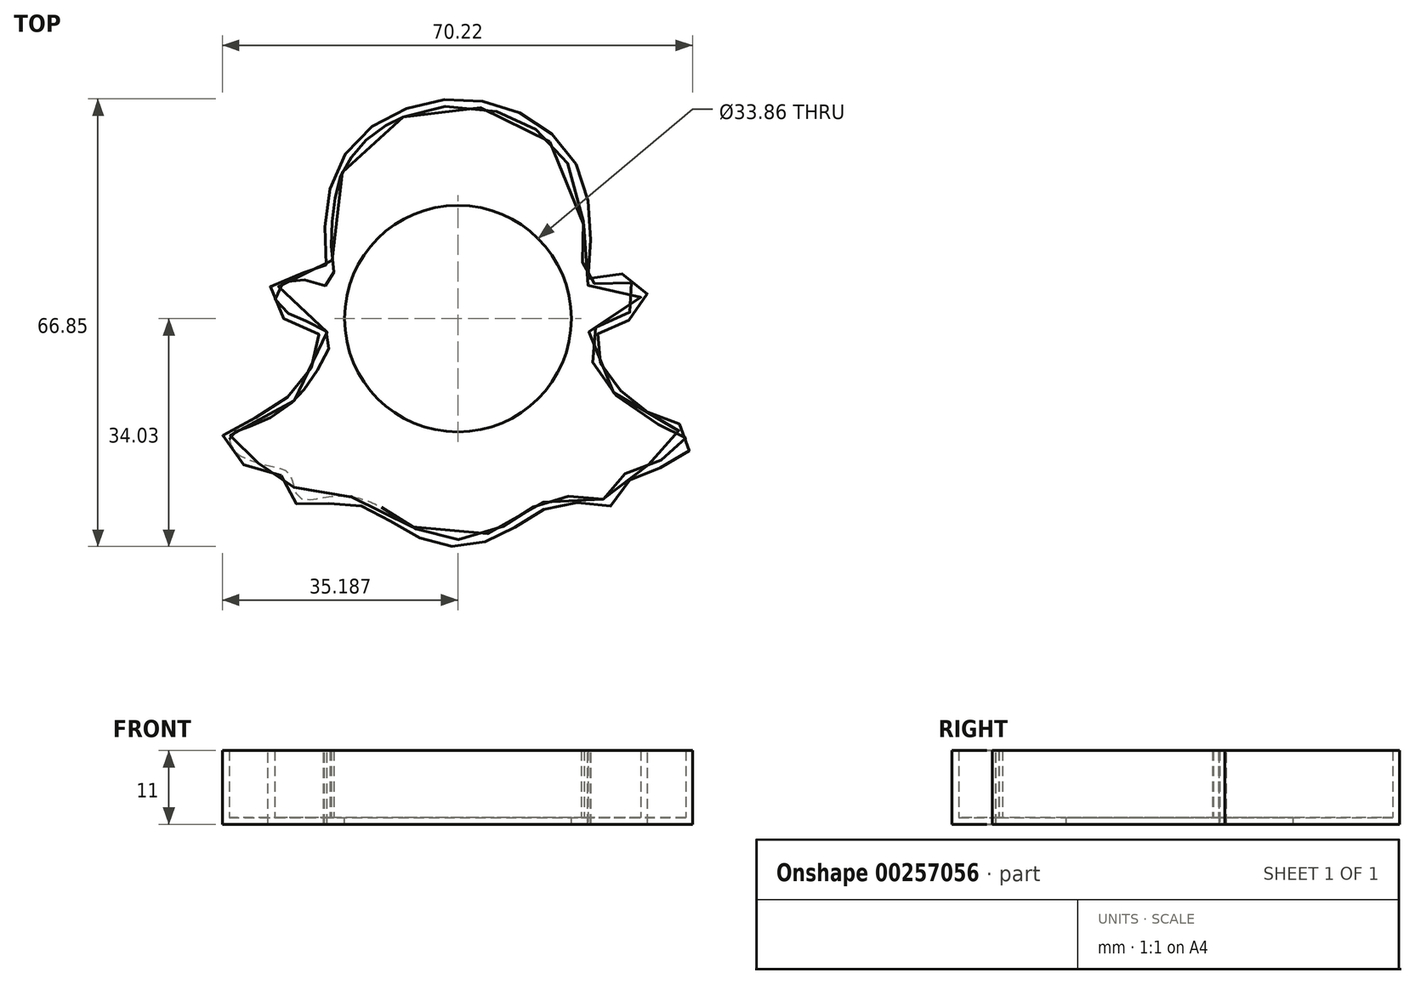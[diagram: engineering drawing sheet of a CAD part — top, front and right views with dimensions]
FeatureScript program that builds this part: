
annotation { "Feature Type Name" : "Feature", "Feature Type Description" : "" }
export const myFeature = defineFeature(function(context is Context, id is Id, definition is map)
    precondition{}
    {
        {
            var Q0;
            Q0=qCreatedBy(makeId("Top.planeOp"),FACE);
            var sketch = newSketch(context, id + "F0", { "sketchPlane" : qUnion([Q0])});
            skFitSpline(sketch, "E0", {"points": [v(3.38, 30.13) * mm, v(1.43, 29.22) * mm, v(-1.52, 27.22) * mm, v(-3.73, 24.97) * mm, v(-5.58, 22.16) * mm, v(-6.38, 19.91) * mm, v(-7.07, 16.23) * mm, v(-7.31, 12.96) * mm, v(-7.22, 8.74) * mm, v(-7.15, 5.54) * mm, v(-8.7, 4.92) * mm, v(-11.6, 5.85) * mm, v(-14.4, 5.54) * mm, v(-15.8, 3.5) * mm, v(-14.95, 1.56) * mm, v(-12.7, 0.26) * mm, v(-10.5, -0.63) * mm, v(-7.93, -2.11) * mm, v(-7.62, -4.06) * mm, v(-9.05, -7.09) * mm, v(-11.09, -10.2) * mm, v(-12.33, -11.65) * mm, v(-14.42, -13.48) * mm, v(-18.32, -15.76) * mm, v(-20.22, -16.3) * mm, v(-21.5, -16.8) * mm, v(-22.14, -17.2) * mm, v(-22.6, -17.69) * mm, v(-22.48, -18.57) * mm, v(-22.12, -19.35) * mm, v(-21.65, -19.92) * mm, v(-21.28, -20.24) * mm, v(-20.78, -20.56) * mm, v(-20.06, -20.9) * mm, v(-18.98, -21.32) * mm, v(-17.82, -21.7) * mm, v(-16.93, -21.92) * mm, v(-16.09, -22.1) * mm, v(-14.96, -22.38) * mm, v(-14.29, -22.62) * mm, v(-13.53, -23.33) * mm, v(-13.13, -24.4) * mm, v(-12.87, -25.45) * mm, v(-12, -26.83) * mm, v(-10.17, -27) * mm, v(-9.12, -26.8) * mm, v(-7.3, -26.52) * mm, v(-4.87, -26.55) * mm, v(-2.83, -26.94) * mm, v(-1.35, -27.46) * mm, v(0.63, -28.45) * mm, v(2.23, -29.52) * mm, v(4.2, -30.82) * mm, v(5.93, -31.7) * mm, v(7.93, -32.53) * mm, v(10.28, -33) * mm, v(13.94, -32.78) * mm, v(16.6, -31.88) * mm, v(18.33, -31.03) * mm, v(19.8, -30.18) * mm, v(21.07, -29.3) * mm, v(22.52, -28.34) * mm, v(24.1, -27.53) * mm, v(26, -26.87) * mm, v(27.55, -26.58) * mm, v(28.72, -26.48) * mm, v(30.27, -26.49) * mm, v(31.82, -26.7) * mm, v(33.48, -26.99) * mm, v(34.9, -26.8) * mm, v(35.9, -25.21) * mm, v(36.5, -23.2) * mm, v(37.72, -22.36) * mm, v(39.55, -21.93) * mm, v(41.7, -21.24) * mm, v(43.87, -20.37) * mm, v(44.84, -19.87) * mm, v(45.49, -18.42) * mm, v(45.5, -17.45) * mm, v(44.69, -16.8) * mm, v(43.73, -16.5) * mm, v(41.95, -15.97) * mm, v(40.1, -15.2) * mm, v(36.62, -12.82) * mm, v(34.56, -10.76) * mm, v(33.11, -8.96) * mm, v(32.14, -7.39) * mm, v(31.25, -5.74) * mm, v(30.43, -3.31) * mm, v(31.4, -1.76) * mm, v(33.1, -0.88) * mm, v(34.66, -0.29) * mm, v(36.06, 0.34) * mm, v(37.83, 1.4) * mm, v(38.86, 2.91) * mm, v(38.52, 4.37) * mm, v(37.3, 5.41) * mm, v(35.44, 5.74) * mm, v(33.82, 5.6) * mm, v(32.05, 5.23) * mm, v(30.7, 5.02) * mm, v(30.02, 5.79) * mm, v(30.04, 7.14) * mm, v(30.24, 8.85) * mm, v(30.31, 10.44) * mm, v(30.4, 13.46) * mm, v(30.25, 15.21) * mm, v(29.37, 20.27) * mm, v(27.21, 24.22) * mm, v(25.52, 26.17) * mm, v(23.68, 27.91) * mm, v(21.52, 29.26) * mm, v(19.62, 30.18) * mm, v(17.2, 31) * mm, v(13.28, 31.72) * mm, v(10.37, 31.78) * mm, v(7.49, 31.36) * mm, v(5.24, 30.78) * mm, v(3.38, 30.13) * mm]});
            skSolve(sketch);
        }
        {
            var Q0;
            Q0=makeQuery(id+"F0.imprint","IMPRINT",FACE,{"disambiguationData":[TD([[makeQuery(id+"F0.imprint","IMPRINT",EDGE,{"derivedFrom":sQuery(id+"F0.wireOp",EDGE,"E0")}),1.0]])]});
            extrude(context, id + "F1", {"entities" : qUnion([Q0]), "depth" : 10 * mm});
        }
        {
            var Q0;
            Q0=makeQuery(id+"F1.opExtrude","CAP_FACE",FACE,{"disambiguationData":[OSD([sQuery(id+"F0.wireOp",EDGE,"E0")])],"isStart":false});
            shell(context, id + "F2", {"entities" : qUnion([Q0]), "thickness" : 1 * mm, "oppositeDirection" : true});
        }
        {
            var Q0;
            {var subQ0=sQuery(id+"F0.wireOp",EDGE,"E0");Q0=makeQuery(id+"F2.opShell","OFFSET_FACE",FACE,{"disambiguationData":[OSD([subQ0]),TDD([makeQuery(id+"F1.opExtrude","CAP_FACE",FACE,{"disambiguationData":[OSD([subQ0])],"isStart":true})])]});}
            var sketch = newSketch(context, id + "F3", { "sketchPlane" : qUnion([Q0])});
            skCircle(sketch, "E1", {"center": v(11.56, 0) * mm, "radius": 16.93 * mm});
            skSolve(sketch);
        }
        {
            var Q0;
            Q0 = qSketchRegion(id + "F3", true);
            extrude(context, id + "F4", {"entities" : qUnion([Q0]), "operationType" : NewBodyOperationType.REMOVE, "oppositeDirection" : true, "depth" : 25.4 * mm});
        }
    });
